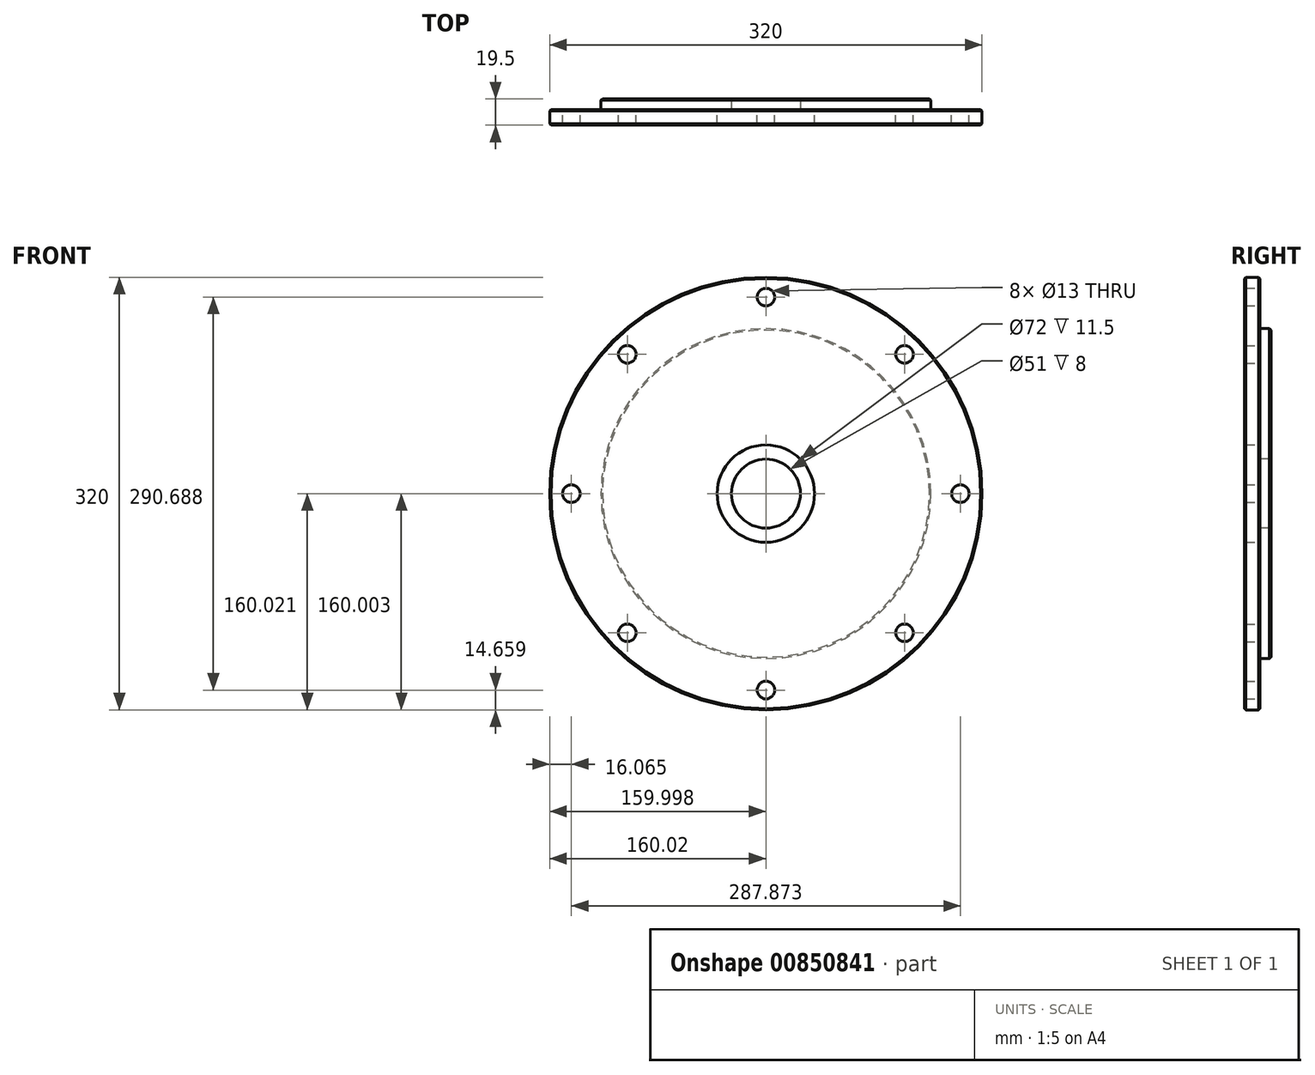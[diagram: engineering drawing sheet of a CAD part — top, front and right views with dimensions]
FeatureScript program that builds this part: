
annotation { "Feature Type Name" : "Feature", "Feature Type Description" : "" }
export const myFeature = defineFeature(function(context is Context, id is Id, definition is map)
    precondition{}
    {
        {
            var Q0;
            Q0=qCreatedBy(makeId("Front.planeOp"),FACE);
            var sketch = newSketch(context, id + "F0", { "sketchPlane" : qUnion([Q0])});
            skCircle(sketch, "E0", {"center": v(-53.13, 5.11) * mm, "radius": 160 * mm});
            skCircle(sketch, "E1", {"center": v(-53.13, 5.11) * mm, "radius": 36 * mm});
            skCircle(sketch, "E2", {"center": v(-53.13, 150.46) * mm, "radius": 6.5 * mm});
            skCircle(sketch, "E3", {"center": v(-155.7, 108.09) * mm, "radius": 6.5 * mm});
            skCircle(sketch, "E4", {"center": v(-197.07, 5.11) * mm, "radius": 6.5 * mm});
            skCircle(sketch, "E5", {"center": v(49.44, 108.08) * mm, "radius": 6.5 * mm});
            skCircle(sketch, "E6", {"center": v(90.8, 5.11) * mm, "radius": 6.5 * mm});
            skCircle(sketch, "E7", {"center": v(49.43, -97.86) * mm, "radius": 6.5 * mm});
            skCircle(sketch, "E8", {"center": v(-53.13, -140.23) * mm, "radius": 6.5 * mm});
            skCircle(sketch, "E9", {"center": v(-155.7, -97.86) * mm, "radius": 6.5 * mm});
            skSolve(sketch);
        }
        {
            var Q0;
            Q0=makeQuery(id+"F0.imprint","IMPRINT",FACE,{"disambiguationData":[TD([[makeQuery(id+"F0.imprint","IMPRINT",EDGE,{"derivedFrom":sQuery(id+"F0.wireOp",EDGE,"E0")}),1.0]])]});
            extrude(context, id + "F1", {"entities" : qUnion([Q0]), "depth" : 11.5 * mm, "offsetDistance" : 25.4 * mm});
        }
        {
            var Q0;
            Q0=makeQuery(id+"F1.opExtrude","CAP_EDGE",EDGE,{"disambiguationData":[OSD([sQuery(id+"F0.wireOp",EDGE,"E0")])],"isStart":true});
            var Q1;
            Q1=makeQuery(id+"F1.opExtrude","CAP_EDGE",EDGE,{"disambiguationData":[OSD([sQuery(id+"F0.wireOp",EDGE,"E0")])],"isStart":false});
            chamfer(context, id + "F2", {"entities" : qUnion([Q0, Q1]), "width" : 1 * mm, "tangentPropagation" : true});
        }
        {
            var Q0;
            Q0=makeQuery(id+"F0.imprint","IMPRINT",FACE,{"disambiguationData":[TD([[makeQuery(id+"F0.imprint","IMPRINT",EDGE,{"derivedFrom":sQuery(id+"F0.wireOp",EDGE,"E0")}),1.0]])]});
            var sketch = newSketch(context, id + "F3", { "sketchPlane" : qUnion([Q0])});
            skCircle(sketch, "E10", {"center": v(-53.11, 5.13) * mm, "radius": 122 * mm});
            skCircle(sketch, "E11", {"center": v(-53.11, 5.13) * mm, "radius": 25.5 * mm});
            skSolve(sketch);
        }
        {
            var Q0;
            Q0=makeQuery(id+"F3.imprint","IMPRINT",FACE,{"disambiguationData":[TD([[makeQuery(id+"F3.imprint","IMPRINT",EDGE,{"derivedFrom":sQuery(id+"F3.wireOp",EDGE,"E11")}),-1.0]])]});
            var Q1;
            Q1=makeQuery(id+"F3.imprint","IMPRINT",FACE,{"disambiguationData":[TD([[makeQuery(id+"F3.imprint","IMPRINT",EDGE,{"derivedFrom":sQuery(id+"F3.wireOp",EDGE,"E10")}),1.0]])]});
            extrude(context, id + "F4", {"entities" : qUnion([Q0, Q1]), "operationType" : NewBodyOperationType.ADD, "oppositeDirection" : true, "depth" : 8 * mm, "offsetDistance" : 25.4 * mm});
        }
        {
            var Q0;
            Q0=makeQuery(id+"F4.opExtrude","CAP_EDGE",EDGE,{"disambiguationData":[OSD([sQuery(id+"F3.wireOp",EDGE,"E10")])],"isStart":false});
            chamfer(context, id + "F5", {"entities" : qUnion([Q0]), "width" : 1 * mm, "tangentPropagation" : true});
        }
    });
